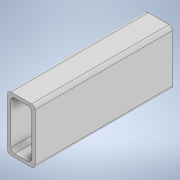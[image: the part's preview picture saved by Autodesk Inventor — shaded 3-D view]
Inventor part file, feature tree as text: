
AUTODESK INVENTOR PART (.ipt)
format: ipt  version: 2020 (Build 240168000, 168)  size: 117,760 bytes
history: native  units: in
note: dims shown in document units (in); Inventor stores cm internally (conversion verified against a paired STEP export)
features: extrude x1, sketch x1
ambient origin geometry x8: Origin, YZ Plane, XZ Plane, XY Plane, X Axis, Y Axis, Z Axis, Center Point
bodies: Solid1 (feature_tree)
feature tree (2):
  extrude  "Extrusion1"  Depth=1.0in
  sketch  "Sketch1"  dims[d0=2.0in d1=1.0in d2=0.125in d3=0.125in d4=0.125in d5=0.125in d6=0.125in d7=0.125in d8=0.125in d9=0.125in d10=0.125in d11=5.0in d12=0.0in]
